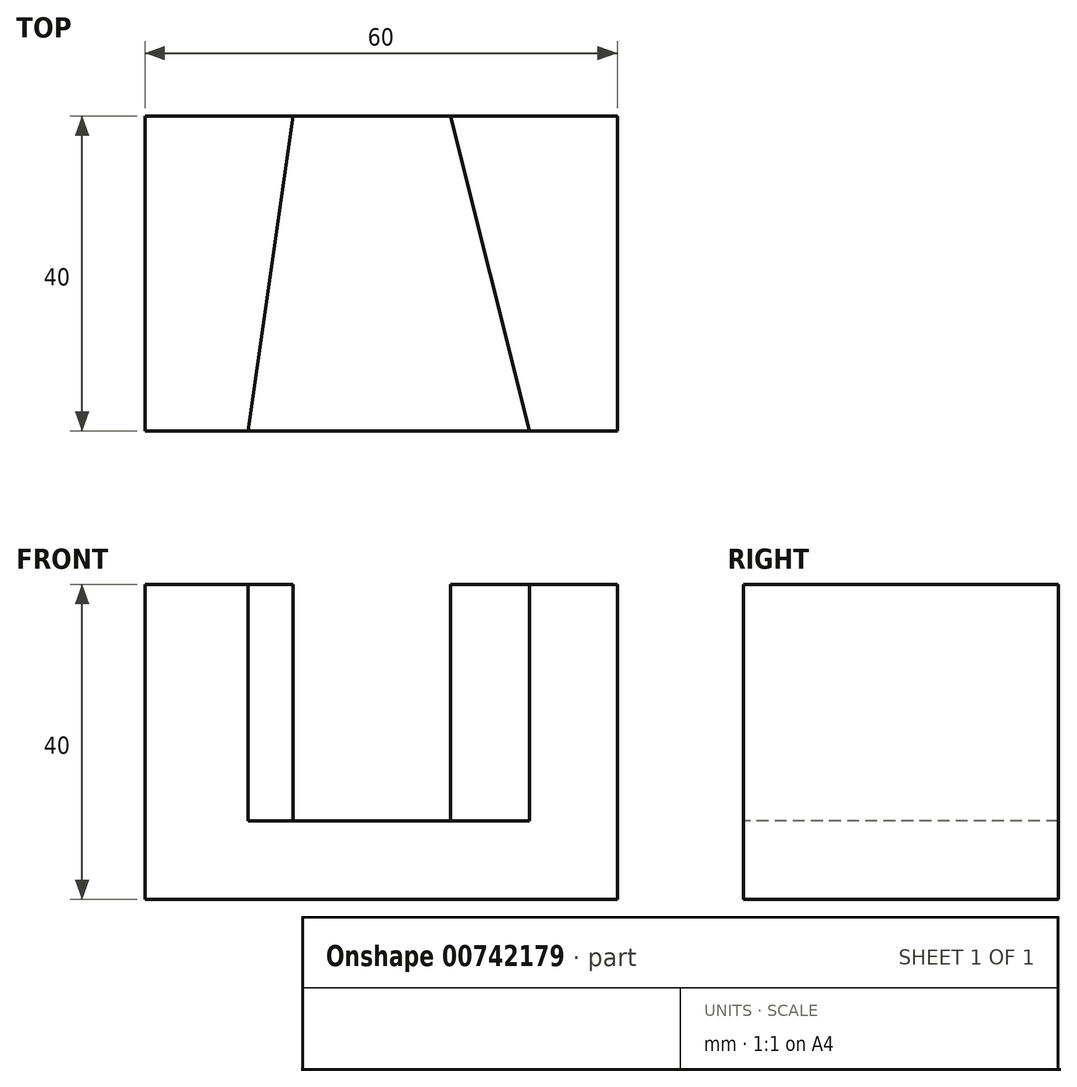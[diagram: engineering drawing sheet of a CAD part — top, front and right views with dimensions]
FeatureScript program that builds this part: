
annotation { "Feature Type Name" : "Feature", "Feature Type Description" : "" }
export const myFeature = defineFeature(function(context is Context, id is Id, definition is map)
    precondition{}
    {
        {
            var Q0;
            Q0=qCreatedBy(makeId("Front.planeOp"),FACE);
            var sketch = newSketch(context, id + "F0", { "sketchPlane" : qUnion([Q0])});
            skLineSegment(sketch, "E0.bottom", {"start": v(-29.54, -40) * mm, "end": v(30.46, -40) * mm});
            skLineSegment(sketch, "E0.top", {"start": v(-29.54, 0) * mm, "end": v(30.46, 0) * mm});
            skLineSegment(sketch, "E0.left", {"start": v(-29.54, -40) * mm, "end": v(-29.54, 0) * mm});
            skLineSegment(sketch, "E0.right", {"start": v(30.46, -40) * mm, "end": v(30.46, 0) * mm});
            skSolve(sketch);
        }
        {
            var Q0;
            Q0=makeQuery(id+"F0.imprint","IMPRINT",FACE,{"disambiguationData":[TD([[makeQuery(id+"F0.imprint","IMPRINT",EDGE,{"derivedFrom":sQuery(id+"F0.wireOp",EDGE,"E0.bottom")}),1.0]])]});
            extrude(context, id + "F1", {"entities" : qUnion([Q0]), "depth" : 40 * mm, "offsetDistance" : 25 * mm});
        }
        {
            var Q0;
            Q0=makeQuery(id+"F1.opExtrude","SWEPT_FACE",FACE,{"disambiguationData":[OSD([sQuery(id+"F0.wireOp",EDGE,"E0.top")])]});
            var sketch = newSketch(context, id + "F2", { "sketchPlane" : qUnion([Q0])});
            skLineSegment(sketch, "E1", {"start": v(-10.7, 0) * mm, "end": v(9.3, 0) * mm});
            skLineSegment(sketch, "E2", {"start": v(-16.43, -40) * mm, "end": v(19.33, -40) * mm});
            skLineSegment(sketch, "E3", {"start": v(-10.7, 0) * mm, "end": v(-16.43, -40) * mm});
            skLineSegment(sketch, "E4", {"start": v(9.3, 0) * mm, "end": v(19.33, -40) * mm});
            skSolve(sketch);
        }
        {
            var Q0;
            Q0=makeQuery(id+"F2.imprint","IMPRINT",FACE,{"disambiguationData":[TD([[makeQuery(id+"F2.imprint","IMPRINT",EDGE,{"derivedFrom":sQuery(id+"F2.wireOp",EDGE,"E1")}),-1.0]])]});
            extrude(context, id + "F3", {"entities" : qUnion([Q0]), "operationType" : NewBodyOperationType.REMOVE, "oppositeDirection" : true, "depth" : 30 * mm, "offsetDistance" : 25 * mm});
        }
    });
